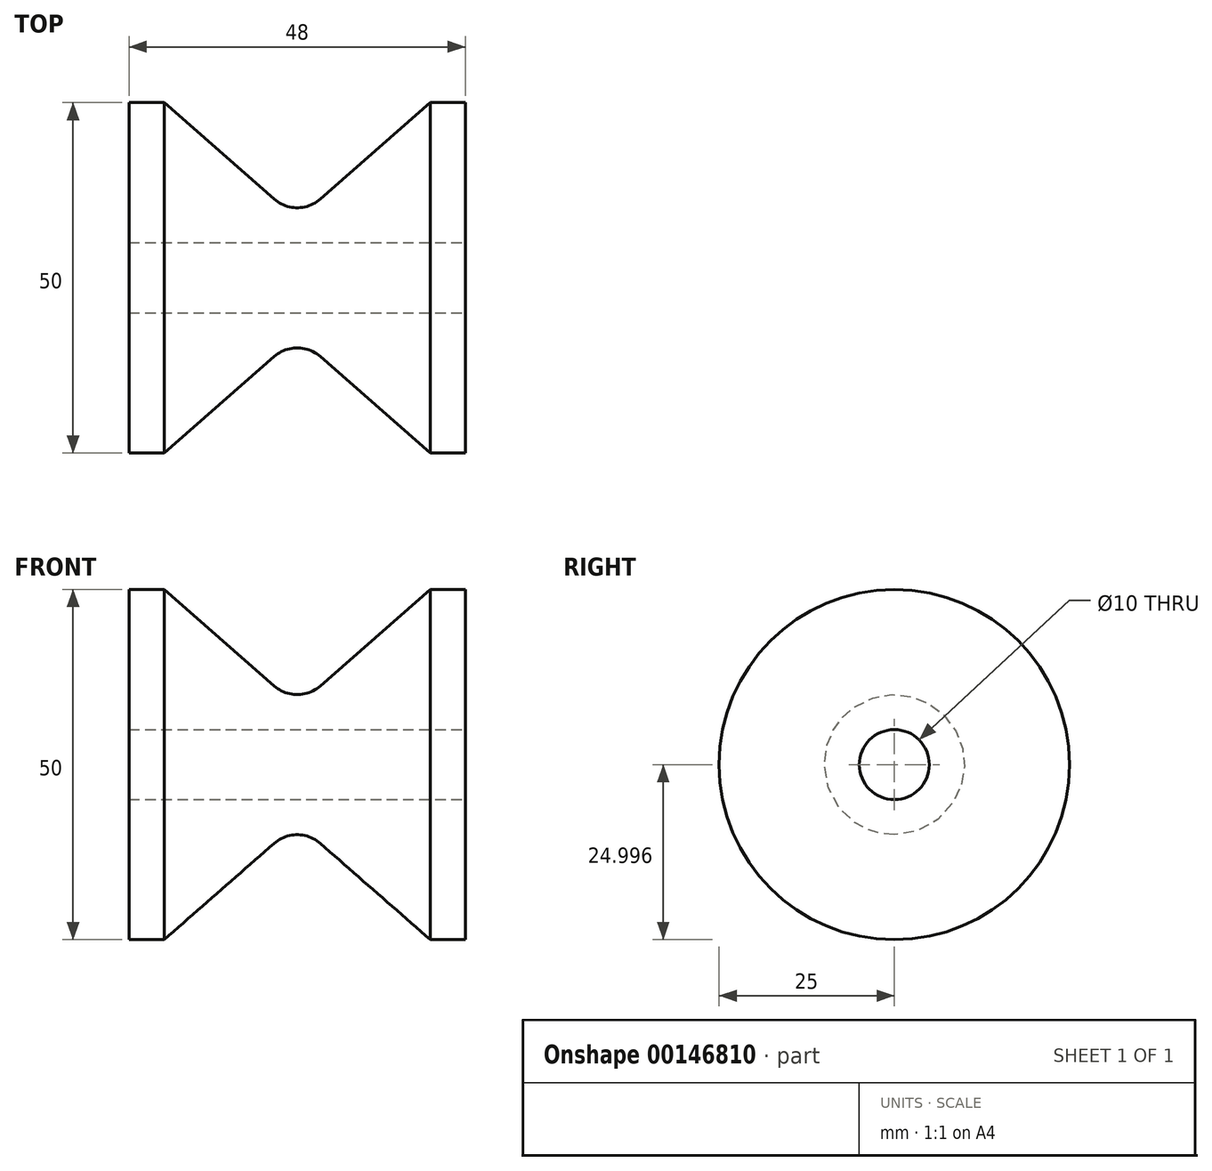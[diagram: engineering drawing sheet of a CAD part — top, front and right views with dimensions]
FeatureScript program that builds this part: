
annotation { "Feature Type Name" : "Feature", "Feature Type Description" : "" }
export const myFeature = defineFeature(function(context is Context, id is Id, definition is map)
    precondition{}
    {
        {
            var Q0;
            Q0=qCreatedBy(makeId("Front.planeOp"),FACE);
            var sketch = newSketch(context, id + "F0", { "sketchPlane" : qUnion([Q0])});
            skLineSegment(sketch, "E0.bottom", {"start": v(-24, 5.16) * mm, "end": v(24, 5.16) * mm});
            skPoint(sketch, "E0.middle", {"position": v(0, 0) * mm});
            skLineSegment(sketch, "E1", {"start": v(-24, 5.16) * mm, "end": v(-24, 25.16) * mm});
            skLineSegment(sketch, "E2", {"start": v(-24, 25.16) * mm, "end": v(-19, 25.16) * mm});
            skLineSegment(sketch, "E3", {"start": v(24, 5.16) * mm, "end": v(24, 25.16) * mm});
            skLineSegment(sketch, "E4", {"start": v(24, 25.16) * mm, "end": v(19, 25.16) * mm});
            skPoint(sketch, "E5.endSnap0", {"position": v(0, 5.16) * mm});
            skArc(sketch, "E6", {"start": v(-3.3, 11.4) * mm, "mid": v(0, 10.16) * mm, "end": v(3.3, 11.4) * mm});
            skLineSegment(sketch, "E7", {"start": v(-19, 25.16) * mm, "end": v(-3.3, 11.4) * mm});
            skLineSegment(sketch, "E8", {"start": v(19, 25.16) * mm, "end": v(3.3, 11.4) * mm});
            skLineSegment(sketch, "E9", {"start": v(0, 5.16) * mm, "end": v(0, 0.16) * mm});
            skLineSegment(sketch, "E10", {"start": v(0, 0.16) * mm, "end": v(-30.31, 0.16) * mm});
            skSolve(sketch);
        }
        {
            var Q0;
            {var subQ0=sQuery(id+"F0.wireOp",EDGE,"E1");Q0=makeQuery(id+"F0.imprint","IMPRINT",FACE,{"disambiguationData":[TD([[makeQuery(id+"F0.imprint","IMPRINT",EDGE,{"derivedFrom":subQ0}),-1.0]])]});}
            var Q1;
            Q1=sQuery(id+"F0.wireOp",EDGE,"E10");
            revolve(context, id + "F1", {"entities" : qUnion([Q0]), "axis" : qUnion([Q1]), "revolveType" : RevolveType.FULL});
        }
    });
